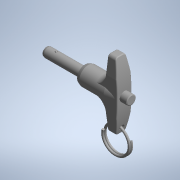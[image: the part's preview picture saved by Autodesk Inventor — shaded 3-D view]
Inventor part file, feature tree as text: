
AUTODESK INVENTOR PART (.ipt)
format: ipt  version: 2022.3 (Build 263350000, 350)  size: 427,520 bytes
history: native  units: mm (DEFAULTED — no unit token found)
features: mirror x2, revolve x1, fillet x1, sweep x1
ambient origin geometry x8: Origin, YZ Plane, XZ Plane, XY Plane, X Axis, Y Axis, Z Axis, Center Point
bodies: Solid1 (feature_tree), Solid2 (feature_tree), Solid3 (feature_tree), Solid4 (feature_tree), Solid5 (feature_tree)
feature tree (5):
  revolve  "Revolve2"  [1 undecoded]
  mirror  "Mirror2"
  mirror  "Mirror1[1]"
  fillet  "Fillet4"  [1 undecoded]
  sweep  "Sweep2"
note: 2 required parameter values undecoded (feature->parameter linkage not recoverable at this tier; creation-order binding heuristic only, values carry confidence <= 0.55)
